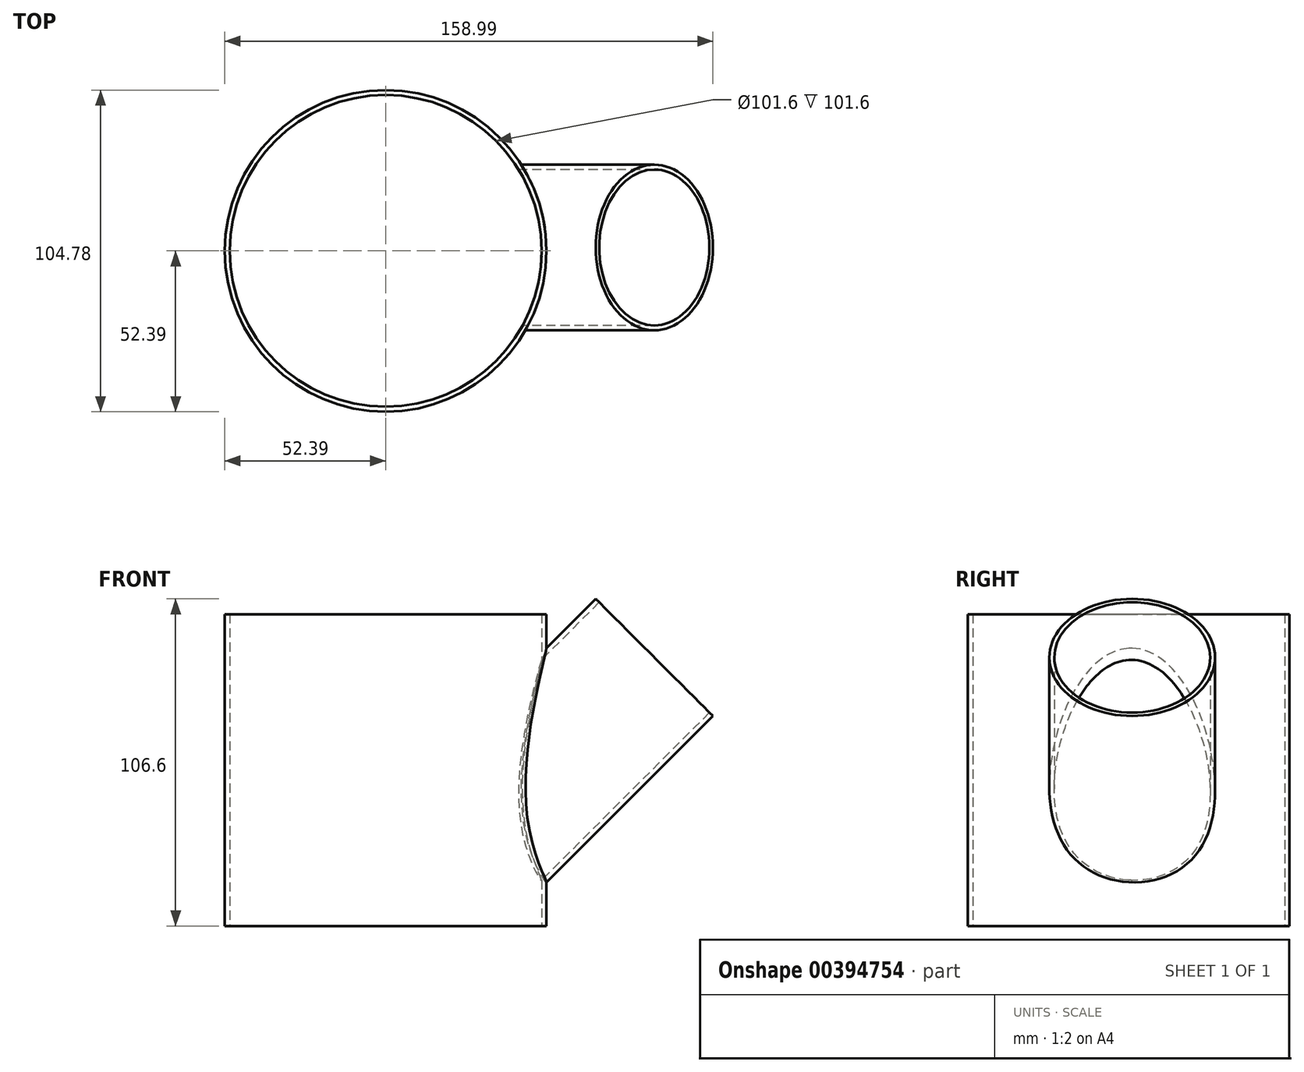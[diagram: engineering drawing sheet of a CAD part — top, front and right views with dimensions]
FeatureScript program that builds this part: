
annotation { "Feature Type Name" : "Feature", "Feature Type Description" : "" }
export const myFeature = defineFeature(function(context is Context, id is Id, definition is map)
    precondition{}
    {
        {
            var Q0;
            Q0=qCreatedBy(makeId("Top.planeOp"),FACE);
            var sketch = newSketch(context, id + "F0", { "sketchPlane" : qUnion([Q0])});
            skCircle(sketch, "E0", {"center": v(0, 0) * mm, "radius": 50.8 * mm});
            skCircle(sketch, "E1", {"center": v(0, 0) * mm, "radius": 52.39 * mm});
            skSolve(sketch);
        }
        {
            var Q0;
            Q0 = qSketchRegion(id + "F0", true);
            extrude(context, id + "F1", {"entities" : qUnion([Q0]), "depth" : 101.6 * mm});
        }
        {
            var Q0;
            Q0=qCreatedBy(makeId("Top.planeOp"),FACE);
            cPlane(context, id + "F2", {"entities" : qUnion([Q0]), "cplaneType" : CPlaneType.OFFSET, "offset" : 50.8 * mm, "width" : 152.4 * mm, "height" : 152.4 * mm});
        }
        {
            var Q0;
            Q0=qCreatedBy(id+"F2.planeOp",FACE);
            var sketch = newSketch(context, id + "F3", { "sketchPlane" : qUnion([Q0])});
            skCircle(sketch, "E2.0", {"center": v(0, 0) * mm, "radius": 52.39 * mm, "construction": true});
            skLineSegment(sketch, "E3", {"start": v(0, 0) * mm, "end": v(52.39, 0) * mm, "construction": true});
            skLineSegment(sketch, "E4", {"start": v(52.39, 0) * mm, "end": v(52.39, 56) * mm});
            skSolve(sketch);
        }
        {
            var Q0;
            Q0=sQuery(id+"F3.wireOp",EDGE,"E4");
            cPlane(context, id + "F4", {"entities" : qUnion([Q0]), "cplaneType" : CPlaneType.LINE_ANGLE, "offset" : 25.4 * mm, "angle" : 45 * degree, "width" : 152.4 * mm, "height" : 152.4 * mm});
        }
        {
            var Q0;
            Q0=qCreatedBy(id+"F4.planeOp",FACE);
            var sketch = newSketch(context, id + "F5", { "sketchPlane" : qUnion([Q0])});
            skPoint(sketch, "E5.0", {"position": v(1.12, 0) * mm});
            skCircle(sketch, "E6", {"center": v(1.12, 0) * mm, "radius": 25.4 * mm});
            skCircle(sketch, "E7", {"center": v(1.12, 0) * mm, "radius": 26.99 * mm});
            skSolve(sketch);
        }
        {
            var Q0;
            Q0=makeQuery(id+"F5.imprint","IMPRINT",FACE,{"disambiguationData":[TD([[makeQuery(id+"F5.imprint","IMPRINT",EDGE,{"derivedFrom":sQuery(id+"F5.wireOp",EDGE,"E6")}),-1.0]])]});
            extrude(context, id + "F6", {"entities" : qUnion([Q0]), "operationType" : NewBodyOperationType.ADD, "depth" : 50.8 * mm, "hasSecondDirection" : true, "secondDirectionOppositeDirection" : true, "secondDirectionDepth" : 50.8 * mm});
        }
        {
            var Q0;
            Q0=makeQuery(id+"F0.imprint","IMPRINT",FACE,{"disambiguationData":[TD([[makeQuery(id+"F0.imprint","IMPRINT",EDGE,{"derivedFrom":sQuery(id+"F0.wireOp",EDGE,"E0")}),1.0]])]});
            extrude(context, id + "F7", {"entities" : qUnion([Q0]), "operationType" : NewBodyOperationType.REMOVE, "endBound" : BoundingType.THROUGH_ALL, "depth" : 271.78 * mm, "hasSecondDirection" : true, "secondDirectionBound" : SecondDirectionBoundingType.THROUGH_ALL, "secondDirectionOppositeDirection" : true, "secondDirectionDepth" : 25.4 * mm});
        }
        {
            var Q0;
            Q0=makeQuery(id+"F5.imprint","IMPRINT",FACE,{"disambiguationData":[TD([[makeQuery(id+"F5.imprint","IMPRINT",EDGE,{"derivedFrom":sQuery(id+"F5.wireOp",EDGE,"E6")}),1.0]])]});
            extrude(context, id + "F8", {"entities" : qUnion([Q0]), "operationType" : NewBodyOperationType.REMOVE, "oppositeDirection" : true, "depth" : 50.8 * mm, "hasSecondDirection" : true, "secondDirectionBound" : SecondDirectionBoundingType.THROUGH_ALL, "secondDirectionOppositeDirection" : false, "secondDirectionDepth" : 25.4 * mm});
        }
    });
